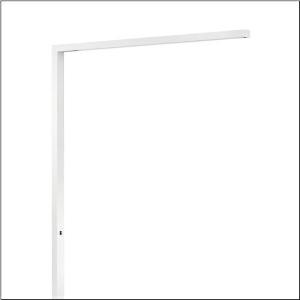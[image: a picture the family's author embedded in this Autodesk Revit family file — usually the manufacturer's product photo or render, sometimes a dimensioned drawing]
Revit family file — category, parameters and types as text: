
# Revit family: silica_r__11_floor_5mx51bs3wzk00002xx_06fb
name_source: partatom
category: Lighting Fixtures
units: mm (PartAtom-declared; Revit-internal decimal feet)

## family parameters
Cut with Voids When Loaded = No
Host = Face
Light Source = No
Part Type = Normal
Room Calculation Point = No
Round Connector Dimension = Use Diameter
Shared = No

## types (1)
- --- (1 x LED, 3960 lm / 8500 lm, 24.4 W / 54.9 W, 4000K)
    Apparent Load = 79 VA
    CIE Flux Codes = 82 97 100 100 100 / - - - 0 100
    Color Rendering = 80
    Color Temperature = 4000K
    Default Elevation = 1800 mm
    Description = Silica® 11 Floor, floorstanding luminaire, of PMMA, primary optical cover: cover panel, of PMMA, light emission: indirect/direct distribution, primary light characteristic: symmetric, installation type: not mounted, LED, rated luminous flux: 12.460lm, luminous efficacy: 157lm/W, light colour: 840, colour temperature: 4000K, daylight-dependent control, mains connection: 230V, AC, 50Hz, connection cable pre-assembled, cable length: 3m, rated input power: 79W, luminaire head, rectangular, rounded, of aluminium, coated, traffic white (RAL 9016), supporting column, angular, of aluminium, coated, traffic white (RAL 9016), baseplate, of steel, coated, traffic white (RAL 9016), length: 1.316mm, width: 65mm, protection rating (complete): IP20, insulation class (complete): insulation class I (protective earthing), certification: CE, permissible operating ambient temperature: 0..+35°C, standard: EN 50419, packaging unit: 1 piece
    Height = 40 mm  [stored 0.131234 ft]
    Lamp = 1 x LED
    Lamp Light Flux = 3960 lm / 8500 lm
    Lamp Power = 24.4 W / 54.9 W
    Lamp count = 1
    Length = 1317 mm
    Luminous efficacy = 157 lm/W
    Manufacturer = Siteco
    ModVariant = No
    Model = 5MX51BS3WZK00002XX
    Mounting Place = Floor
    Mounting Type = Freestanding
    Number of Poles = 1
    OnlyDefault = Yes
    Power Factor = 1
    Product Name = Silica® 11 Floor
    Product group = floorstanding luminaire
    ProductGroupID = 1301
    Protection Class = Protection class I
    Protection Degree = IP 20
    RLX_Detail_Level = 1
    RLX_Emergency_Light_Flux = 0 lm
    RLX_Emergency_Type = 0
    RLX_Emergency_Type_DB = No
    RlxData = <blob elided: 18117 chars, md5=7ea6f36d>
    Socket = socket
    Standby Power = 0 W
    System Light Flux = 12460 lm
    System Power = 79 W
    Type Comments = factory setting: direct and indirect light
    Type Image = l_1004655.jpg
    URL = http://relux.com
    VarID = @adj_138206
    Voltage = 0 V
    Weight = 0.00 kg
    Width = 65 mm

note: [stored X ft] marks values corroborated as IEEE doubles in the binary element streams (Revit-internal decimal feet)

## geometry (parser evidence)
native form markers: Blend x4, Sweep x18
no freeform markers — native parametric forms only
